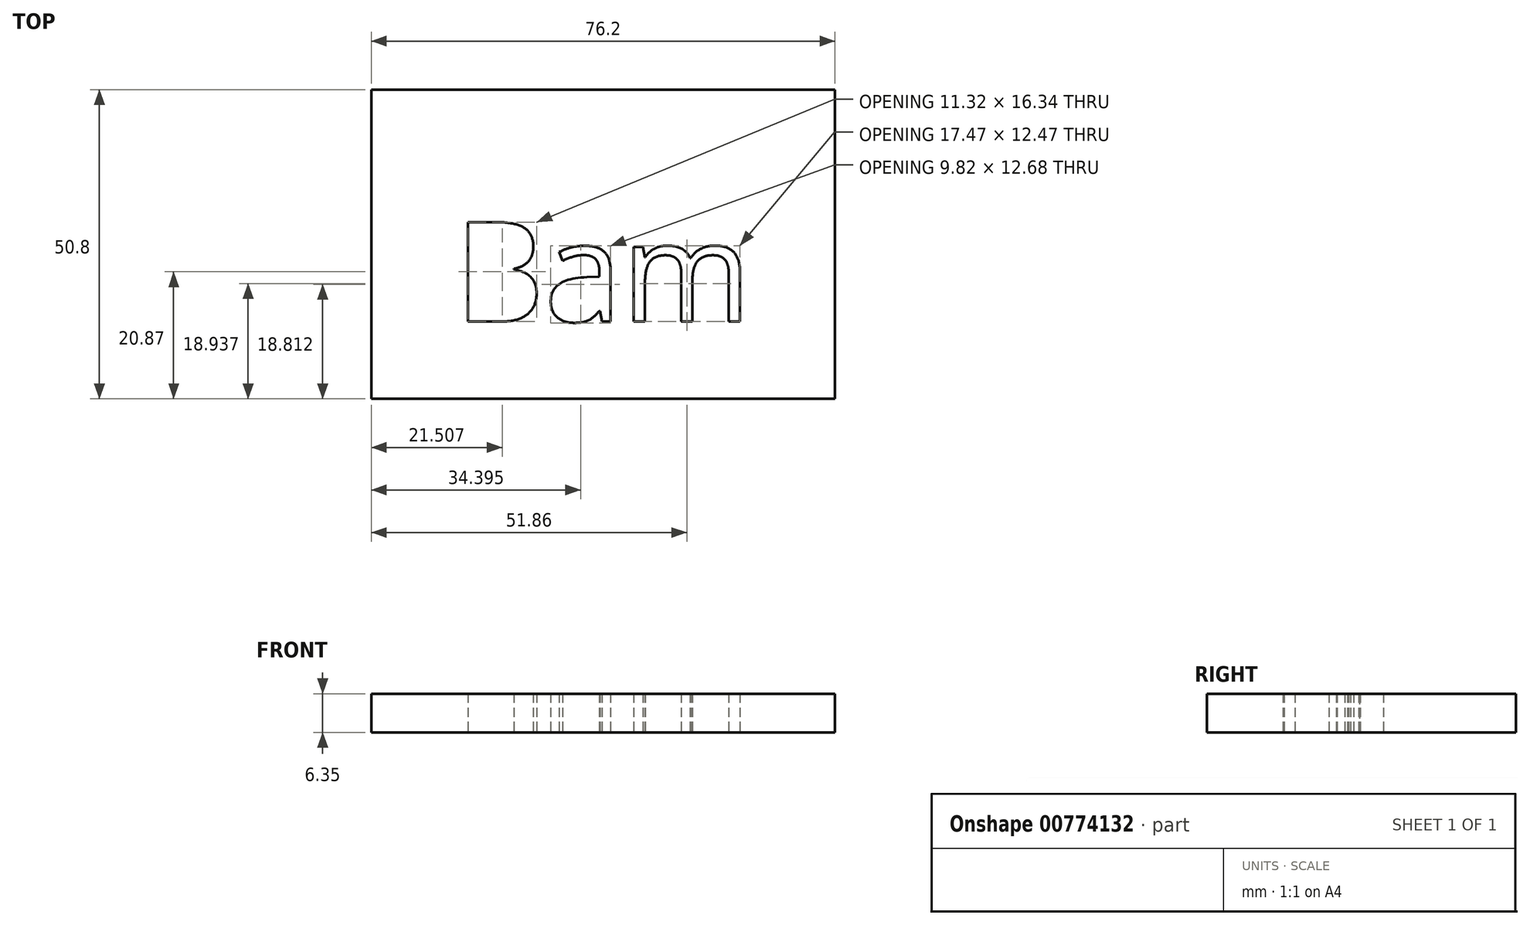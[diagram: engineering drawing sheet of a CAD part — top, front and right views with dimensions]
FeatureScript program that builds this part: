
annotation { "Feature Type Name" : "Feature", "Feature Type Description" : "" }
export const myFeature = defineFeature(function(context is Context, id is Id, definition is map)
    precondition{}
    {
        {
            var Q0;
            Q0=qCreatedBy(makeId("Top.planeOp"),FACE);
            var sketch = newSketch(context, id + "F0", { "sketchPlane" : qUnion([Q0])});
            skLineSegment(sketch, "E0.bottom", {"start": v(-38.1, 25.4) * mm, "end": v(38.1, 25.4) * mm});
            skLineSegment(sketch, "E0.top", {"start": v(-38.1, -25.4) * mm, "end": v(38.1, -25.4) * mm});
            skLineSegment(sketch, "E0.left", {"start": v(-38.1, 25.4) * mm, "end": v(-38.1, -25.4) * mm});
            skLineSegment(sketch, "E0.right", {"start": v(38.1, 25.4) * mm, "end": v(38.1, -25.4) * mm});
            skPoint(sketch, "E0.middle", {"position": v(0, 0) * mm});
            skText(sketch, "E1", { "text": "Bam", "fontName": "OpenSans-Regular.ttf"});
            const initialGuessF0  = {"E1": [-0.0245, -0.0127, 1, 0, 0.01648]};
            skSetInitialGuess(sketch, initialGuessF0);
            skSolve(sketch);
        }
        {
            var Q0;
            Q0=makeQuery(id+"F0.imprint","IMPRINT",FACE,{"disambiguationData":[TD([[makeQuery(id+"F0.imprint","IMPRINT",EDGE,{"derivedFrom":sQuery(id+"F0.wireOp",EDGE,"E0.bottom")}),-1.0]])]});
            extrude(context, id + "F1", {"entities" : qUnion([Q0]), "depth" : 6.35 * mm, "offsetDistance" : 25.4 * mm});
        }
    });
